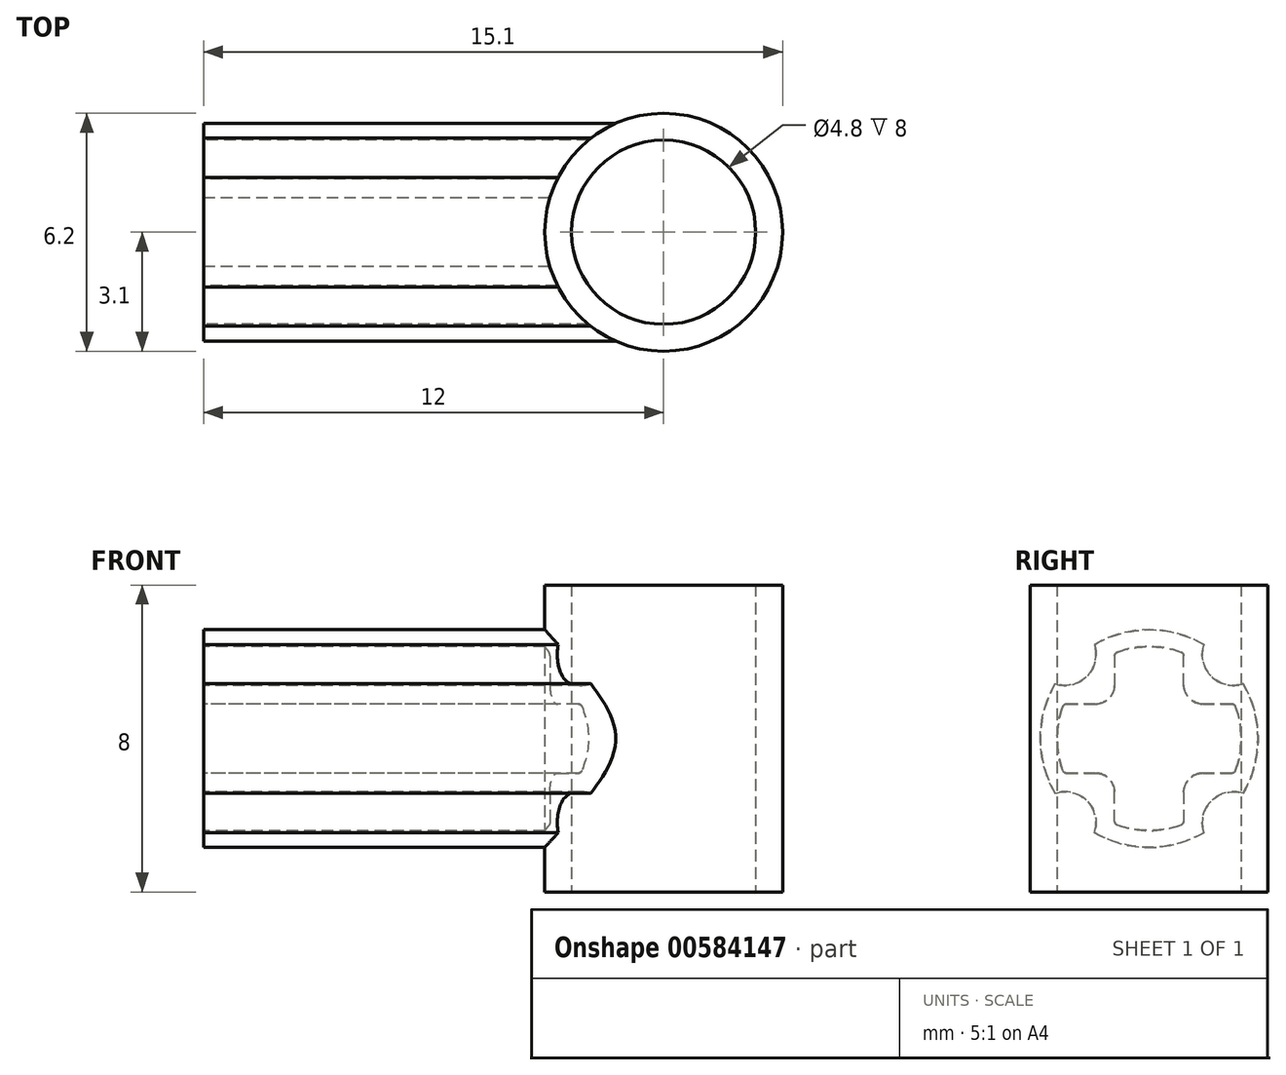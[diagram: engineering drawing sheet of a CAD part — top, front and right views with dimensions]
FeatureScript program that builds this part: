
annotation { "Feature Type Name" : "Feature", "Feature Type Description" : "" }
export const myFeature = defineFeature(function(context is Context, id is Id, definition is map)
    precondition{}
    {
        {
            var Q0;
            Q0=qCreatedBy(makeId("Top.planeOp"),FACE);
            var sketch = newSketch(context, id + "F0", { "sketchPlane" : qUnion([Q0])});
            skArc(sketch, "E0", {"start": v(0, 2.4) * mm, "mid": v(-2.4, 0) * mm, "end": v(0, -2.4) * mm});
            skArc(sketch, "E1", {"start": v(0, 3.1) * mm, "mid": v(-3.1, 0) * mm, "end": v(0, -3.1) * mm});
            skLineSegment(sketch, "E2", {"start": v(0, 3.1) * mm, "end": v(0, 2.4) * mm});
            skLineSegment(sketch, "E3", {"start": v(0, -2.4) * mm, "end": v(0, -3.1) * mm});
            skSolve(sketch);
        }
        {
            var Q0;
            Q0 = qSketchRegion(id + "F0", true);
            extrude(context, id + "F1", {"entities" : qUnion([Q0]), "depth" : 4 * mm, "offsetDistance" : 25 * mm});
        }
        {
            var Q0;
            Q0=makeQuery(id+"F1.opExtrude","CAP_VERTEX",VERTEX,{"disambiguationData":[OSD([sQuery(id+"F0.wireOp",EDGE,"E1"),sQuery(id+"F0.wireOp",EDGE,"E2")])],"isStart":false});
            var Q1;
            Q1=makeQuery(id+"F1.opExtrude","CAP_VERTEX",VERTEX,{"disambiguationData":[OSD([sQuery(id+"F0.wireOp",EDGE,"E0"),sQuery(id+"F0.wireOp",EDGE,"E2")])],"isStart":false});
            var Q2;
            Q2=makeQuery(id+"F1.opExtrude","CAP_VERTEX",VERTEX,{"disambiguationData":[OSD([sQuery(id+"F0.wireOp",EDGE,"E0"),sQuery(id+"F0.wireOp",EDGE,"E2")])],"isStart":true});
            cPlane(context, id + "F2", {"entities" : qUnion([Q0, Q1, Q2]), "cplaneType" : CPlaneType.THREE_POINT, "offset" : 25 * mm, "width" : 150 * mm, "height" : 150 * mm});
        }
        {
            var Q0;
            Q0=qCreatedBy(id+"F2.planeOp",FACE);
            cPlane(context, id + "F3", {"entities" : qUnion([Q0]), "cplaneType" : CPlaneType.OFFSET, "offset" : 12 * mm, "width" : 150 * mm, "height" : 150 * mm});
        }
        {
            var Q0;
            Q0=qCreatedBy(id+"F3.planeOp",FACE);
            var sketch = newSketch(context, id + "F4", { "sketchPlane" : qUnion([Q0])});
            skLineSegment(sketch, "E4.0", {"start": v(2.4, 0) * mm, "end": v(3.1, 0) * mm, "construction": true});
            skLineSegment(sketch, "E4.1", {"start": v(-3.1, 0) * mm, "end": v(-2.4, 0) * mm, "construction": true});
            skLineSegment(sketch, "E5", {"start": v(-2.4, 0) * mm, "end": v(2.4, 0) * mm, "construction": true});
            skLineSegment(sketch, "E6", {"start": v(0, 1.65) * mm, "end": v(0, -0.27) * mm, "construction": true});
            skPoint(sketch, "E6.startSnap0", {"position": v(0, 0) * mm});
            skLineSegment(sketch, "E7", {"start": v(0, 5.29) * mm, "end": v(0, 1.3) * mm, "construction": true});
            skLineSegment(sketch, "E8.0", {"start": v(-0.9, 1.4) * mm, "end": v(-0.9, 2.16) * mm});
            skArc(sketch, "E8.1", {"start": v(-0.9, 2.16) * mm, "mid": v(-0.88, 2.21) * mm, "end": v(-0.83, 2.25) * mm});
            skArc(sketch, "E8.2", {"start": v(-0.83, 2.25) * mm, "mid": v(0, 2.4) * mm, "end": v(0.83, 2.25) * mm});
            skArc(sketch, "E8.3", {"start": v(0.83, 2.25) * mm, "mid": v(0.88, 2.21) * mm, "end": v(0.9, 2.16) * mm});
            skLineSegment(sketch, "E8.4", {"start": v(0.9, 2.16) * mm, "end": v(0.9, 1.4) * mm});
            skArc(sketch, "E8.5", {"start": v(0.9, 1.4) * mm, "mid": v(1.05, 1.05) * mm, "end": v(1.4, 0.9) * mm});
            skLineSegment(sketch, "E8.6", {"start": v(1.4, 0.9) * mm, "end": v(2.16, 0.9) * mm});
            skArc(sketch, "E8.7", {"start": v(-1.4, 0.9) * mm, "mid": v(-1.05, 1.05) * mm, "end": v(-0.9, 1.4) * mm});
            skLineSegment(sketch, "E8.8", {"start": v(-2.16, 0.9) * mm, "end": v(-1.4, 0.9) * mm});
            skArc(sketch, "E8.10", {"start": v(-2.25, 0.83) * mm, "mid": v(-2.21, 0.88) * mm, "end": v(-2.16, 0.9) * mm});
            skArc(sketch, "E8.11", {"start": v(2.16, 0.9) * mm, "mid": v(2.21, 0.88) * mm, "end": v(2.25, 0.83) * mm});
            skArc(sketch, "E8.12", {"start": v(2.25, 0.83) * mm, "mid": v(2.36, 0.42) * mm, "end": v(2.4, 0) * mm});
            skArc(sketch, "E9", {"start": v(-2.4, 0) * mm, "mid": v(-2.36, 0.42) * mm, "end": v(-2.25, 0.83) * mm});
            skArc(sketch, "E10.MirrorCS", {"start": v(-2.25, -0.83) * mm, "mid": v(-2.21, -0.88) * mm, "end": v(-2.16, -0.9) * mm});
            skArc(sketch, "E11.MirrorCS", {"start": v(2.16, -0.9) * mm, "mid": v(2.21, -0.88) * mm, "end": v(2.25, -0.83) * mm});
            skArc(sketch, "E12.MirrorCS", {"start": v(0.83, -2.25) * mm, "mid": v(0.88, -2.21) * mm, "end": v(0.9, -2.16) * mm});
            skArc(sketch, "E13.MirrorCS", {"start": v(-0.9, -2.16) * mm, "mid": v(-0.88, -2.21) * mm, "end": v(-0.83, -2.25) * mm});
            skLineSegment(sketch, "E14.MirrorCS", {"start": v(-2.16, -0.9) * mm, "end": v(-1.4, -0.9) * mm});
            skArc(sketch, "E15.MirrorCS", {"start": v(2.25, -0.83) * mm, "mid": v(2.36, -0.42) * mm, "end": v(2.4, 0) * mm});
            skArc(sketch, "E16.MirrorCS", {"start": v(-2.4, 0) * mm, "mid": v(-2.36, -0.42) * mm, "end": v(-2.25, -0.83) * mm});
            skLineSegment(sketch, "E17.MirrorCS", {"start": v(0, -1.65) * mm, "end": v(0, 0.27) * mm, "construction": true});
            skLineSegment(sketch, "E18.MirrorCS", {"start": v(0.9, -2.16) * mm, "end": v(0.9, -1.4) * mm});
            skLineSegment(sketch, "E19.MirrorCS", {"start": v(-0.9, -1.4) * mm, "end": v(-0.9, -2.16) * mm});
            skLineSegment(sketch, "E20.MirrorCS", {"start": v(0, -5.29) * mm, "end": v(0, -1.3) * mm, "construction": true});
            skArc(sketch, "E21.MirrorCS", {"start": v(-1.4, -0.9) * mm, "mid": v(-1.05, -1.05) * mm, "end": v(-0.9, -1.4) * mm});
            skArc(sketch, "E22.MirrorCS", {"start": v(0.9, -1.4) * mm, "mid": v(1.05, -1.05) * mm, "end": v(1.4, -0.9) * mm});
            skArc(sketch, "E23.MirrorCS", {"start": v(-0.83, -2.25) * mm, "mid": v(0, -2.4) * mm, "end": v(0.83, -2.25) * mm});
            skLineSegment(sketch, "E24.MirrorCS", {"start": v(1.4, -0.9) * mm, "end": v(2.16, -0.9) * mm});
            skArc(sketch, "E25", {"start": v(-2.84, 0) * mm, "mid": v(-2.74, 0.74) * mm, "end": v(-2.45, 1.43) * mm});
            skLineSegment(sketch, "E26", {"start": v(0, 0) * mm, "end": v(-2.67, 2.67) * mm, "construction": true});
            skArc(sketch, "E27", {"start": v(-2.45, 1.43) * mm, "mid": v(-2, 1.4) * mm, "end": v(-1.62, 1.62) * mm});
            skArc(sketch, "E28.MirrorCS", {"start": v(-1.43, 2.45) * mm, "mid": v(-1.4, 2) * mm, "end": v(-1.62, 1.62) * mm});
            skArc(sketch, "E29.MirrorCS", {"start": v(0, 2.84) * mm, "mid": v(-0.74, 2.74) * mm, "end": v(-1.43, 2.45) * mm});
            skArc(sketch, "E30.MirrorCS", {"start": v(0, 2.84) * mm, "mid": v(0.74, 2.74) * mm, "end": v(1.43, 2.45) * mm});
            skArc(sketch, "E31.MirrorCS", {"start": v(2.45, 1.43) * mm, "mid": v(2, 1.4) * mm, "end": v(1.62, 1.62) * mm});
            skArc(sketch, "E32.MirrorCS", {"start": v(1.43, 2.45) * mm, "mid": v(1.4, 2) * mm, "end": v(1.62, 1.62) * mm});
            skArc(sketch, "E33.MirrorCS", {"start": v(2.84, 0) * mm, "mid": v(2.74, 0.74) * mm, "end": v(2.45, 1.43) * mm});
            skArc(sketch, "E34.MirrorCS", {"start": v(-2.84, 0) * mm, "mid": v(-2.74, -0.74) * mm, "end": v(-2.45, -1.43) * mm});
            skArc(sketch, "E35.MirrorCS", {"start": v(-2.45, -1.43) * mm, "mid": v(-2, -1.4) * mm, "end": v(-1.62, -1.62) * mm});
            skArc(sketch, "E36.MirrorCS", {"start": v(-1.43, -2.45) * mm, "mid": v(-1.4, -2) * mm, "end": v(-1.62, -1.62) * mm});
            skArc(sketch, "E37.MirrorCS", {"start": v(0, -2.84) * mm, "mid": v(-0.74, -2.74) * mm, "end": v(-1.43, -2.45) * mm});
            skArc(sketch, "E38.MirrorCS", {"start": v(0, -2.84) * mm, "mid": v(0.74, -2.74) * mm, "end": v(1.43, -2.45) * mm});
            skArc(sketch, "E39.MirrorCS", {"start": v(1.43, -2.45) * mm, "mid": v(1.4, -2) * mm, "end": v(1.62, -1.62) * mm});
            skArc(sketch, "E40.MirrorCS", {"start": v(2.45, -1.43) * mm, "mid": v(2, -1.4) * mm, "end": v(1.62, -1.62) * mm});
            skArc(sketch, "E41.MirrorCS", {"start": v(2.84, 0) * mm, "mid": v(2.74, -0.74) * mm, "end": v(2.45, -1.43) * mm});
            skSolve(sketch);
        }
        {
            var Q0;
            Q0=makeQuery(id+"F1.opExtrude","SWEPT_BODY",BODY,{"disambiguationData":[OSD([sQuery(id+"F0.wireOp",EDGE,"E0"),sQuery(id+"F0.wireOp",EDGE,"E1"),sQuery(id+"F0.wireOp",EDGE,"E2"),sQuery(id+"F0.wireOp",EDGE,"E3")])]});
            var Q1;
            Q1=makeQuery(id+"F1.opExtrude","SWEPT_FACE",FACE,{"disambiguationData":[OSD([sQuery(id+"F0.wireOp",EDGE,"E2")])]});
            mirror(context, id + "F5", {"operationType" : NewBodyOperationType.ADD, "entities" : qUnion([Q0]), "mirrorPlane" : qUnion([Q1])});
        }
        {
            var Q0;
            Q0=makeQuery(id+"F1.opExtrude","SWEPT_BODY",BODY,{"disambiguationData":[OSD([sQuery(id+"F0.wireOp",EDGE,"E0"),sQuery(id+"F0.wireOp",EDGE,"E1"),sQuery(id+"F0.wireOp",EDGE,"E2"),sQuery(id+"F0.wireOp",EDGE,"E3")])]});
            var Q1;
            {var subQ0=makeQuery(id+"F1.opExtrude","CAP_FACE",FACE,{"disambiguationData":[OSD([sQuery(id+"F0.wireOp",EDGE,"E0"),sQuery(id+"F0.wireOp",EDGE,"E1"),sQuery(id+"F0.wireOp",EDGE,"E2"),sQuery(id+"F0.wireOp",EDGE,"E3")])],"isStart":true});Q1=makeQuery(id+"F5.boolean.opBoolean","MERGE",FACE,{"derivedFrom":[subQ0,makeQuery(id+"F5.opPattern","COPY",FACE,{"derivedFrom":subQ0,"instanceName":"1"})]});}
            mirror(context, id + "F6", {"operationType" : NewBodyOperationType.ADD, "entities" : qUnion([Q0]), "mirrorPlane" : qUnion([Q1])});
        }
        {
            var Q0;
            Q0=makeQuery(id+"F4.imprint","IMPRINT",FACE,{"disambiguationData":[TD([[makeQuery(id+"F4.imprint","IMPRINT",EDGE,{"derivedFrom":sQuery(id+"F4.wireOp",EDGE,"E8.0")}),1.0]])]});
            var Q1;
            Q1=makeQuery(id+"F1.opExtrude","SWEPT_BODY",BODY,{"disambiguationData":[OSD([sQuery(id+"F0.wireOp",EDGE,"E0"),sQuery(id+"F0.wireOp",EDGE,"E1"),sQuery(id+"F0.wireOp",EDGE,"E2"),sQuery(id+"F0.wireOp",EDGE,"E3")])]});
            extrude(context, id + "F7", {"entities" : qUnion([Q0]), "operationType" : NewBodyOperationType.ADD, "endBound" : BoundingType.UP_TO_BODY, "oppositeDirection" : true, "depth" : 25 * mm, "endBoundEntityBody" : qUnion([Q1]), "offsetDistance" : 25 * mm});
        }
    });
